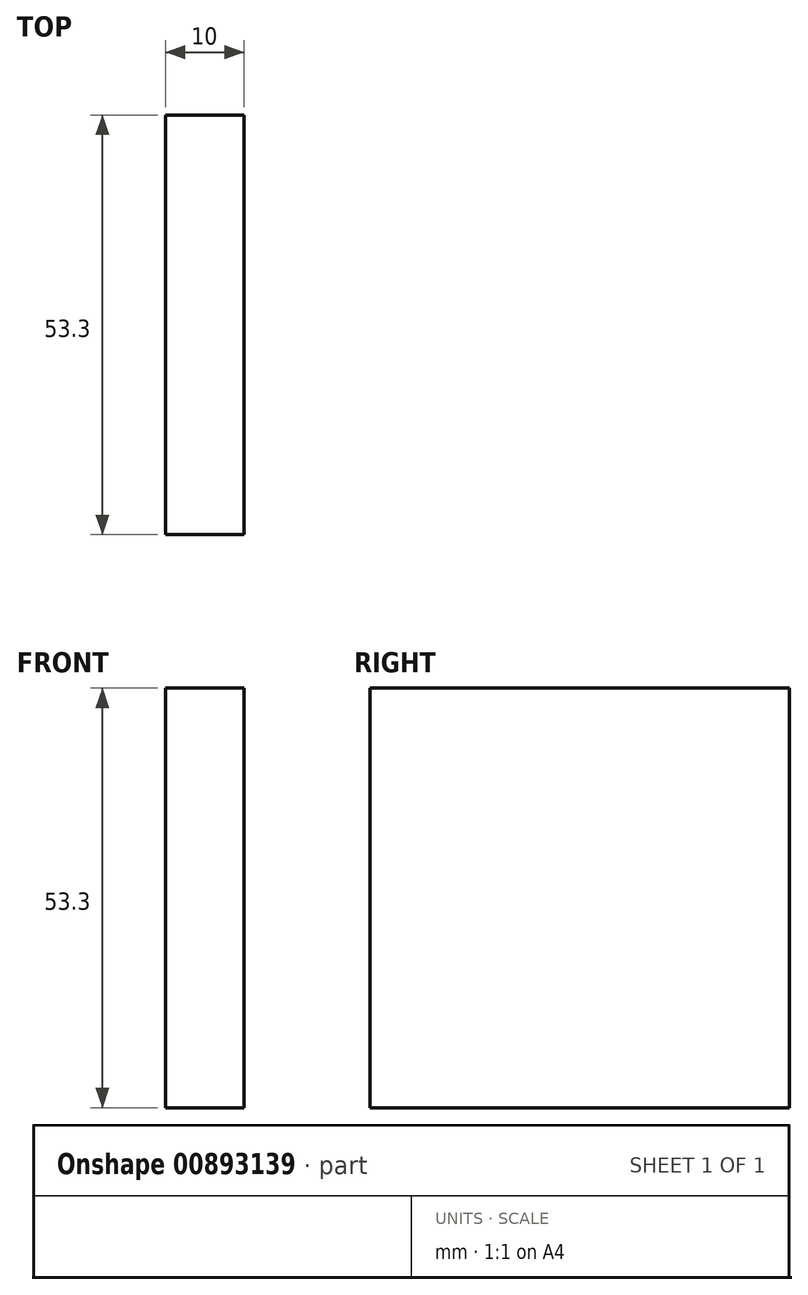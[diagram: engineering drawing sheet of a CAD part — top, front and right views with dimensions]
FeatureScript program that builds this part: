
annotation { "Feature Type Name" : "Feature", "Feature Type Description" : "" }
export const myFeature = defineFeature(function(context is Context, id is Id, definition is map)
    precondition{}
    {
        {
            var Q0;
            Q0=qCreatedBy(makeId("Right.planeOp"),FACE);
            var sketch = newSketch(context, id + "F0", { "sketchPlane" : qUnion([Q0])});
            skPoint(sketch, "E0.endSnap0", {"position": v(3.75, 0) * mm});
            skPoint(sketch, "E0.endSnap1", {"position": v(0, 3.75) * mm});
            skPoint(sketch, "E1.endSnap0", {"position": v(3.75, 22.5) * mm});
            skLineSegment(sketch, "E2.0", {"start": v(0, 37.9) * mm, "end": v(22.5, 37.9) * mm});
            skLineSegment(sketch, "E3.0", {"start": v(22.5, -15.4) * mm, "end": v(0, -15.4) * mm});
            skLineSegment(sketch, "E4.0", {"start": v(-15.4, 15) * mm, "end": v(-15.4, 7.5) * mm});
            skLineSegment(sketch, "E5.0", {"start": v(37.9, 22.5) * mm, "end": v(37.9, 0) * mm});
            skLineSegment(sketch, "E6", {"start": v(22.5, 37.9) * mm, "end": v(37.9, 37.9) * mm});
            skLineSegment(sketch, "E7", {"start": v(37.9, 37.9) * mm, "end": v(37.9, 22.5) * mm});
            skLineSegment(sketch, "E8", {"start": v(0, 37.9) * mm, "end": v(-15.4, 37.9) * mm});
            skLineSegment(sketch, "E9", {"start": v(-15.4, 37.9) * mm, "end": v(-15.4, 15) * mm});
            skLineSegment(sketch, "E10", {"start": v(0, -15.4) * mm, "end": v(-15.4, -15.4) * mm});
            skLineSegment(sketch, "E11", {"start": v(-15.4, -15.4) * mm, "end": v(-15.4, 7.5) * mm});
            skLineSegment(sketch, "E12", {"start": v(22.5, -15.4) * mm, "end": v(37.9, -15.4) * mm});
            skLineSegment(sketch, "E13", {"start": v(37.9, -15.4) * mm, "end": v(37.9, 0) * mm});
            skSolve(sketch);
        }
        {
            var Q0;
            Q0=makeQuery(id+"F0.imprint","IMPRINT",FACE,{"disambiguationData":[TD([[makeQuery(id+"F0.imprint","IMPRINT",EDGE,{"derivedFrom":sQuery(id+"F0.wireOp",EDGE,"B36j9lZX-R2AH-HQyz-juRm-mwcovSKJ9z7z")}),-1.0]])]});
            var Q1;
            Q1=makeQuery(id+"F0.imprint","IMPRINT",FACE,{"disambiguationData":[TD([[makeQuery(id+"F0.imprint","IMPRINT",EDGE,{"derivedFrom":sQuery(id+"F0.wireOp",EDGE,"E2.0")}),-1.0]])]});
            extrude(context, id + "F1", {"entities" : qUnion([Q0, Q1]), "oppositeDirection" : true, "depth" : 10 * mm, "offsetDistance" : 25 * mm});
        }
    });
